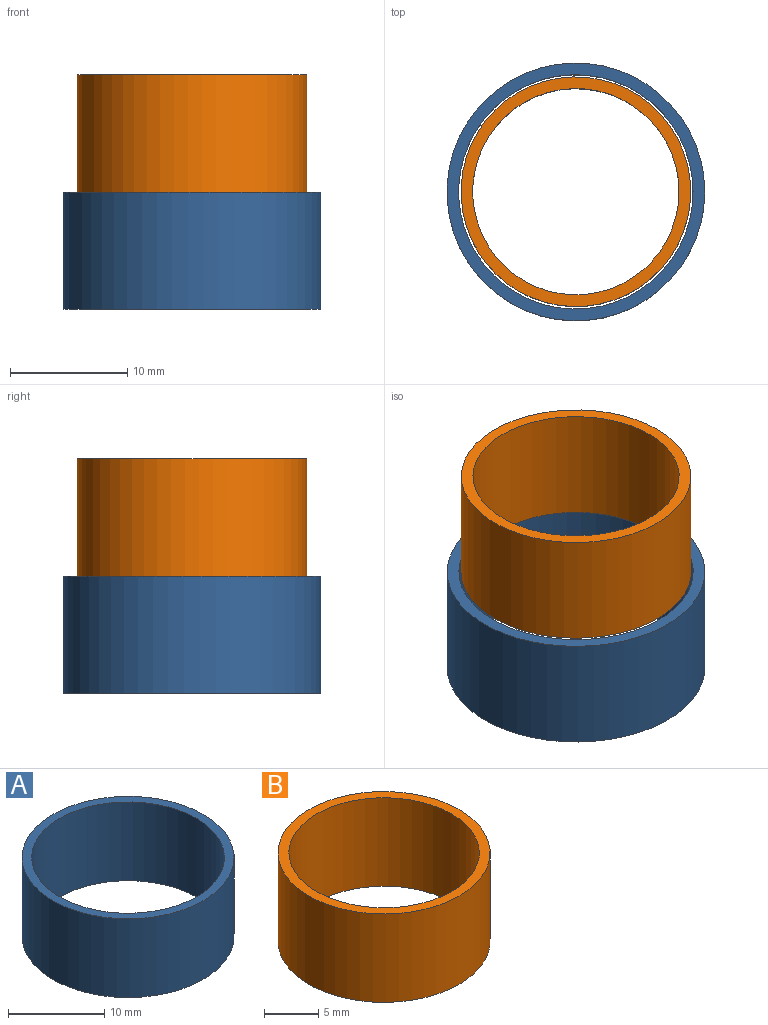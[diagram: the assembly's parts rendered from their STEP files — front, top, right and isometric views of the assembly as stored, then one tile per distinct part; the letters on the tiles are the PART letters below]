
ASSEMBLY  parts=2 mates=1
PART A: 4 faces, bbox 22x22x10 mm
  f0: cylinder r=10mm len=20mm, axis (0,0,-1), area 628.3mm2, adj f2,f3
  f1: cylinder r=11mm len=22mm, axis (0,0,-1), area 691.2mm2, adj f2,f3
  f2: plane 22x22mm, normal (0,0,1), area 66mm2, adj f0,f1
  f3: plane 22x22mm, normal (0,0,-1), area 66mm2, adj f0,f1
PART B: 4 faces, bbox 19.6x19.6x10 mm
  f0: cylinder r=8.8mm len=17.6mm, axis (0,0,-1), area 552.9mm2, adj f2,f3
  f1: cylinder r=9.8mm len=19.6mm, axis (0,0,-1), area 615.8mm2, adj f2,f3
  f2: plane 19.6x19.6mm, normal (0,0,1), area 58.4mm2, adj f0,f1
  f3: plane 19.6x19.6mm, normal (0,0,-1), area 58.4mm2, adj f0,f1
PLACE A at identity fixed
PLACE B rot(axis=(1,0,0),180deg) t=(0,0,20)mm
MATE slider A.f1 <-> B.f1  axis (0,0,1) through (0,0,10)mm
